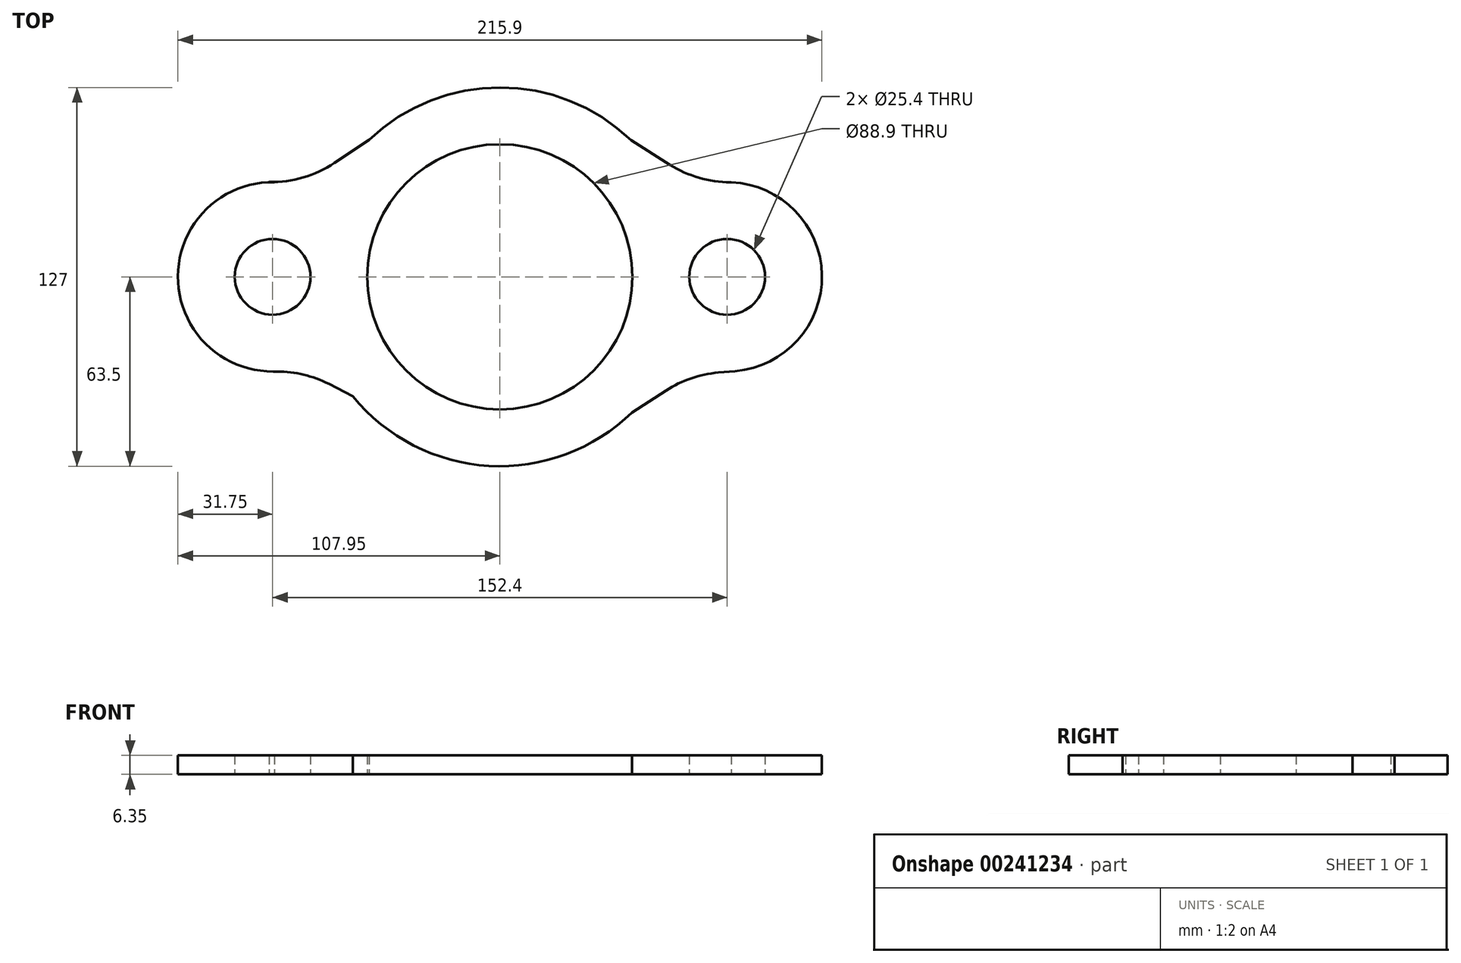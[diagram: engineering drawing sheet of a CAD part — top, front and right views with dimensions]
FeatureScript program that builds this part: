
annotation { "Feature Type Name" : "Feature", "Feature Type Description" : "" }
export const myFeature = defineFeature(function(context is Context, id is Id, definition is map)
    precondition{}
    {
        {
            var Q0;
            Q0=qCreatedBy(makeId("Top.planeOp"),FACE);
            var sketch = newSketch(context, id + "F0", { "sketchPlane" : qUnion([Q0])});
            skCircle(sketch, "E0", {"center": v(0, 0) * mm, "radius": 44.45 * mm});
            skCircle(sketch, "E1", {"center": v(76.2, 0) * mm, "radius": 12.7 * mm});
            skCircle(sketch, "E2", {"center": v(-76.2, 0) * mm, "radius": 12.7 * mm});
            skArc(sketch, "E3", {"start": v(-49.27, -40.06) * mm, "mid": v(-3.67, -63.4) * mm, "end": v(44.32, -45.48) * mm});
            skArc(sketch, "E4", {"start": v(78.88, -31.64) * mm, "mid": v(107.91, 1.53) * mm, "end": v(75.83, 31.75) * mm});
            skArc(sketch, "E5", {"start": v(-75.61, 31.74) * mm, "mid": v(-107.95, 0.21) * mm, "end": v(-76.04, -31.75) * mm});
            skLineSegment(sketch, "E6", {"start": v(77.6, 31.72) * mm, "end": v(77.31, 31.72) * mm});
            skLineSegment(sketch, "E7", {"start": v(44.01, 45.77) * mm, "end": v(57, 37.59) * mm});
            skPoint(sketch, "E8.orphan", {"position": v(55.01, 31.72) * mm});
            skPoint(sketch, "E9.visualSharp", {"position": v(66.3, 31.72) * mm});
            skArc(sketch, "E9.filletArc", {"start": v(57, 37.59) * mm, "mid": v(66.74, 33.22) * mm, "end": v(77.31, 31.72) * mm});
            skLineSegment(sketch, "E10", {"start": v(78.88, -31.64) * mm, "end": v(73.2, -32.12) * mm});
            skLineSegment(sketch, "E11", {"start": v(44.32, -45.48) * mm, "end": v(55.74, -38.1) * mm});
            skPoint(sketch, "E12.visualSharp", {"position": v(63.73, -32.92) * mm});
            skArc(sketch, "E12.filletArc", {"start": v(73.2, -32.12) * mm, "mid": v(64.1, -34.03) * mm, "end": v(55.74, -38.1) * mm});
            skLineSegment(sketch, "E13", {"start": v(-76.04, -31.75) * mm, "end": v(-74.7, -31.75) * mm});
            skLineSegment(sketch, "E14", {"start": v(-49.27, -40.06) * mm, "end": v(-57.35, -35.93) * mm});
            skPoint(sketch, "E15.orphan", {"position": v(-55, -31.75) * mm});
            skPoint(sketch, "E16.visualSharp", {"position": v(-65.52, -31.75) * mm});
            skArc(sketch, "E16.filletArc", {"start": v(-57.35, -35.93) * mm, "mid": v(-65.77, -32.8) * mm, "end": v(-74.7, -31.75) * mm});
            skLineSegment(sketch, "E17", {"start": v(-77.33, 31.78) * mm, "end": v(-75.61, 31.74) * mm});
            skLineSegment(sketch, "E18", {"start": v(-43.87, 45.91) * mm, "end": v(-55.5, 38.16) * mm});
            skPoint(sketch, "E19.orphan", {"position": v(-55.21, 31.37) * mm});
            skPoint(sketch, "E20.visualSharp", {"position": v(-65.41, 31.56) * mm});
            skArc(sketch, "E20.filletArc", {"start": v(-77.33, 31.78) * mm, "mid": v(-65.92, 33.3) * mm, "end": v(-55.5, 38.16) * mm});
            skArc(sketch, "E21.trimOffspring", {"start": v(44.01, 45.77) * mm, "mid": v(0.1, 63.5) * mm, "end": v(-43.87, 45.91) * mm});
            skSolve(sketch);
        }
        {
            var Q0;
            Q0=makeQuery(id+"F0.imprint","IMPRINT",FACE,{"disambiguationData":[TD([[makeQuery(id+"F0.imprint","IMPRINT",EDGE,{"derivedFrom":sQuery(id+"F0.wireOp",EDGE,"E0")}),-1.0]])]});
            extrude(context, id + "F1", {"entities" : qUnion([Q0]), "depth" : 6.35 * mm});
        }
    });
